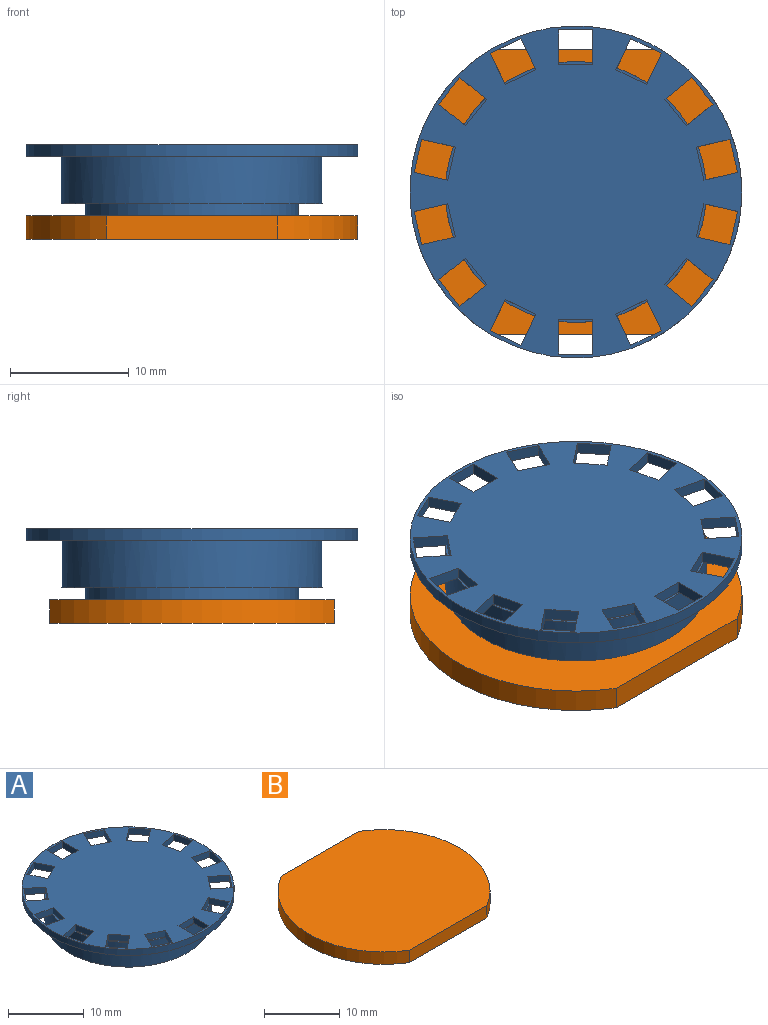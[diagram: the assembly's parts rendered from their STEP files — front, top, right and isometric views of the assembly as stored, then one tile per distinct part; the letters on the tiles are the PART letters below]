
ASSEMBLY  parts=2 mates=1
PART A: 77 faces, bbox 28x28x6 mm
  f0: plane 2.65x1.38mm, normal (0,0,1), area 0.6mm2, adj f16,f18,f19,f60
  f1: plane 2.34x1.9mm, normal (0,0,1), area 0.6mm2, adj f16,f21,f22,f23
  f2: plane 2.83x0.78mm, normal (0,0,1), area 0.6mm2, adj f16,f24,f25,f26
  f3: plane 2.83x0.78mm, normal (0,0,1), area 0.6mm2, adj f16,f27,f28,f29
  f4: plane 2.34x1.9mm, normal (0,0,1), area 0.6mm2, adj f16,f30,f31,f32
  f5: plane 2.65x1.38mm, normal (0,0,1), area 0.6mm2, adj f16,f33,f34,f35
  f6: plane 2.87x0.24mm, normal (0,0,1), area 0.6mm2, adj f16,f36,f37,f38
  f7: plane 2.65x1.38mm, normal (0,0,1), area 0.6mm2, adj f16,f39,f40,f41
  f8: plane 2.34x1.9mm, normal (0,0,1), area 0.6mm2, adj f16,f42,f43,f44
  f9: plane 2.83x0.78mm, normal (0,0,1), area 0.6mm2, adj f16,f45,f46,f47
  f10: plane 2.83x0.78mm, normal (0,0,1), area 0.6mm2, adj f16,f48,f49,f50
  f11: plane 2.34x1.9mm, normal (0,0,1), area 0.6mm2, adj f16,f51,f52,f53
  f12: plane 2.65x1.38mm, normal (0,0,1), area 0.6mm2, adj f16,f54,f55,f56
  f13: plane 2.87x0.24mm, normal (0,0,1), area 0.6mm2, adj f16,f57,f58,f59
  f14: cylinder r=9mm len=18mm, axis (0,0,-1), area 56.5mm2, adj f15,f17
  f15: plane 18x18mm, normal (0,0,-1), area 254.5mm2, adj f14
  f16: cylinder r=11mm len=22mm, axis (0,0,-1), area 276.5mm2, adj f0,f1,f2,f3,f4,f5,f6,f7
  f17: plane 22x22mm, normal (0,0,-1), area 125.7mm2, adj f14,f16
  f18: plane 2.59x1.25mm, normal (-0.43,0.9,0), area 2.9mm2, adj f0,f19,f60,f75
  f19: plane 2.62x1.26mm, normal (0.9,0.43,0), area 2.9mm2, adj f0,f18,f20,f75,f76
  f20: plane 2.59x1.25mm, normal (0.43,-0.9,0), area 2.9mm2, adj f19,f60,f75,f76
  f21: plane 2.27x1.81mm, normal (-0.62,-0.78,0), area 2.9mm2, adj f1,f22,f61,f75,f76
  f22: plane 2.24x1.79mm, normal (-0.78,0.62,0), area 2.9mm2, adj f1,f21,f23,f75
  f23: plane 2.27x1.81mm, normal (0.62,0.78,0), area 2.9mm2, adj f1,f22,f61,f75,f76
  f24: plane 2.83x1mm, normal (-0.22,-0.97,0), area 2.9mm2, adj f2,f25,f62,f75,f76
  f25: plane 2.8x1mm, normal (-0.97,0.22,0), area 2.9mm2, adj f2,f24,f26,f75
  f26: plane 2.83x1mm, normal (0.22,0.97,0), area 2.9mm2, adj f2,f25,f62,f75,f76
  f27: plane 2.83x1mm, normal (0.22,-0.97,0), area 2.9mm2, adj f3,f28,f63,f75,f76
  f28: plane 2.8x1mm, normal (-0.97,-0.22,0), area 2.9mm2, adj f3,f27,f29,f75
  f29: plane 2.83x1mm, normal (-0.22,0.97,0), area 2.9mm2, adj f3,f28,f63,f75,f76
  f30: plane 2.27x1.81mm, normal (0.62,-0.78,0), area 2.9mm2, adj f4,f31,f64,f75,f76
  f31: plane 2.24x1.79mm, normal (-0.78,-0.62,0), area 2.9mm2, adj f4,f30,f32,f75
  f32: plane 2.27x1.81mm, normal (-0.62,0.78,0), area 2.9mm2, adj f4,f31,f64,f75,f76
  f33: plane 2.62x1.26mm, normal (0.9,-0.43,0), area 2.9mm2, adj f5,f34,f65,f75,f76
  f34: plane 2.59x1.25mm, normal (-0.43,-0.9,0), area 2.9mm2, adj f5,f33,f35,f75
  f35: plane 2.62x1.26mm, normal (-0.9,0.43,0), area 2.9mm2, adj f5,f34,f65,f75,f76
  f36: plane 2.91x1mm, normal (1,0,0), area 2.9mm2, adj f6,f37,f66,f75,f76
  f37: plane 2.87x1mm, normal (0,-1,0), area 2.9mm2, adj f6,f36,f38,f75
  f38: plane 2.91x1mm, normal (-1,0,0), area 2.9mm2, adj f6,f37,f66,f75,f76
  f39: plane 2.62x1.26mm, normal (0.9,0.43,0), area 2.9mm2, adj f7,f40,f67,f75,f76
  f40: plane 2.59x1.25mm, normal (0.43,-0.9,0), area 2.9mm2, adj f7,f39,f41,f75
  f41: plane 2.62x1.26mm, normal (-0.9,-0.43,0), area 2.9mm2, adj f7,f40,f67,f75,f76
  f42: plane 2.27x1.81mm, normal (0.62,0.78,0), area 2.9mm2, adj f8,f43,f68,f75,f76
  f43: plane 2.24x1.79mm, normal (0.78,-0.62,0), area 2.9mm2, adj f8,f42,f44,f75
  f44: plane 2.27x1.81mm, normal (-0.62,-0.78,0), area 2.9mm2, adj f8,f43,f68,f75,f76
  f45: plane 2.83x1mm, normal (0.22,0.97,0), area 2.9mm2, adj f9,f46,f69,f75,f76
  f46: plane 2.8x1mm, normal (0.97,-0.22,0), area 2.9mm2, adj f9,f45,f47,f75
  f47: plane 2.83x1mm, normal (-0.22,-0.97,0), area 2.9mm2, adj f9,f46,f69,f75,f76
  f48: plane 2.83x1mm, normal (-0.22,0.97,0), area 2.9mm2, adj f10,f49,f70,f75,f76
  f49: plane 2.8x1mm, normal (0.97,0.22,0), area 2.9mm2, adj f10,f48,f50,f75
  f50: plane 2.83x1mm, normal (0.22,-0.97,0), area 2.9mm2, adj f10,f49,f70,f75,f76
  f51: plane 2.27x1.81mm, normal (-0.62,0.78,0), area 2.9mm2, adj f11,f52,f71,f75,f76
  f52: plane 2.24x1.79mm, normal (0.78,0.62,0), area 2.9mm2, adj f11,f51,f53,f75
  f53: plane 2.27x1.81mm, normal (0.62,-0.78,0), area 2.9mm2, adj f11,f52,f71,f75,f76
  f54: plane 2.62x1.26mm, normal (-0.9,0.43,0), area 2.9mm2, adj f12,f55,f72,f75,f76
  f55: plane 2.59x1.25mm, normal (0.43,0.9,0), area 2.9mm2, adj f12,f54,f56,f75
  f56: plane 2.62x1.26mm, normal (0.9,-0.43,0), area 2.9mm2, adj f12,f55,f72,f75,f76
  f57: plane 2.91x1mm, normal (-1,0,0), area 2.9mm2, adj f13,f58,f73,f75,f76
  f58: plane 2.87x1mm, normal (0,1,0), area 2.9mm2, adj f13,f57,f59,f75
  f59: plane 2.91x1mm, normal (1,0,0), area 2.9mm2, adj f13,f58,f73,f75,f76
  f60: plane 2.62x1.26mm, normal (-0.9,-0.43,0), area 2.9mm2, adj f0,f18,f20,f75,f76
  f61: plane 2.24x1.79mm, normal (0.78,-0.62,0), area 2.9mm2, adj f21,f23,f75,f76
  f62: plane 2.8x1mm, normal (0.97,-0.22,0), area 2.9mm2, adj f24,f26,f75,f76
  f63: plane 2.8x1mm, normal (0.97,0.22,0), area 2.9mm2, adj f27,f29,f75,f76
  f64: plane 2.24x1.79mm, normal (0.78,0.62,0), area 2.9mm2, adj f30,f32,f75,f76
  f65: plane 2.59x1.25mm, normal (0.43,0.9,0), area 2.9mm2, adj f33,f35,f75,f76
  f66: plane 2.87x1mm, normal (0,1,0), area 2.9mm2, adj f36,f38,f75,f76
  f67: plane 2.59x1.25mm, normal (-0.43,0.9,0), area 2.9mm2, adj f39,f41,f75,f76
  f68: plane 2.24x1.79mm, normal (-0.78,0.62,0), area 2.9mm2, adj f42,f44,f75,f76
  f69: plane 2.8x1mm, normal (-0.97,0.22,0), area 2.9mm2, adj f45,f47,f75,f76
  f70: plane 2.8x1mm, normal (-0.97,-0.22,0), area 2.9mm2, adj f48,f50,f75,f76
  f71: plane 2.24x1.79mm, normal (-0.78,-0.62,0), area 2.9mm2, adj f51,f53,f75,f76
  f72: plane 2.59x1.25mm, normal (-0.43,-0.9,0), area 2.9mm2, adj f54,f56,f75,f76
  f73: plane 2.87x1mm, normal (0,-1,0), area 2.9mm2, adj f57,f59,f75,f76
  f74: cylinder r=14mm len=28mm, axis (0,0,-1), area 88mm2, adj f75,f76
  f75: plane 28x28mm, normal (0,0,1), area 499mm2, adj f18,f19,f20,f21,f22,f23,f24,f25
  f76: plane 28x28mm, normal (0,0,-1), area 127.3mm2, adj f16,f19,f20,f21,f23,f24,f26,f27
PART B: 6 faces, bbox 28x24x2 mm
  f0: plane 14.42x2mm, normal (0,1,0), area 28.8mm2, adj f1,f3,f4,f5
  f1: cylinder r=14mm len=24mm, axis (0,0,-1), area 57.7mm2, adj f0,f2,f4,f5
  f2: plane 14.42x2mm, normal (0,-1,0), area 28.8mm2, adj f1,f3,f4,f5
  f3: cylinder r=14mm len=24mm, axis (0,0,-1), area 57.7mm2, adj f0,f2,f4,f5
  f4: plane 28x24mm, normal (0,0,1), area 576.7mm2, adj f0,f1,f2,f3
  f5: plane 28x24mm, normal (0,0,-1), area 576.7mm2, adj f0,f1,f2,f3
PLACE A t=(-0.17,0.61,7.37)mm
PLACE B t=(-0.17,0.61,5.37)mm
MATE fastened B.f1 <-> A.f14  axis (0,0,1) through (-0.17,0.61,7.37)mm
